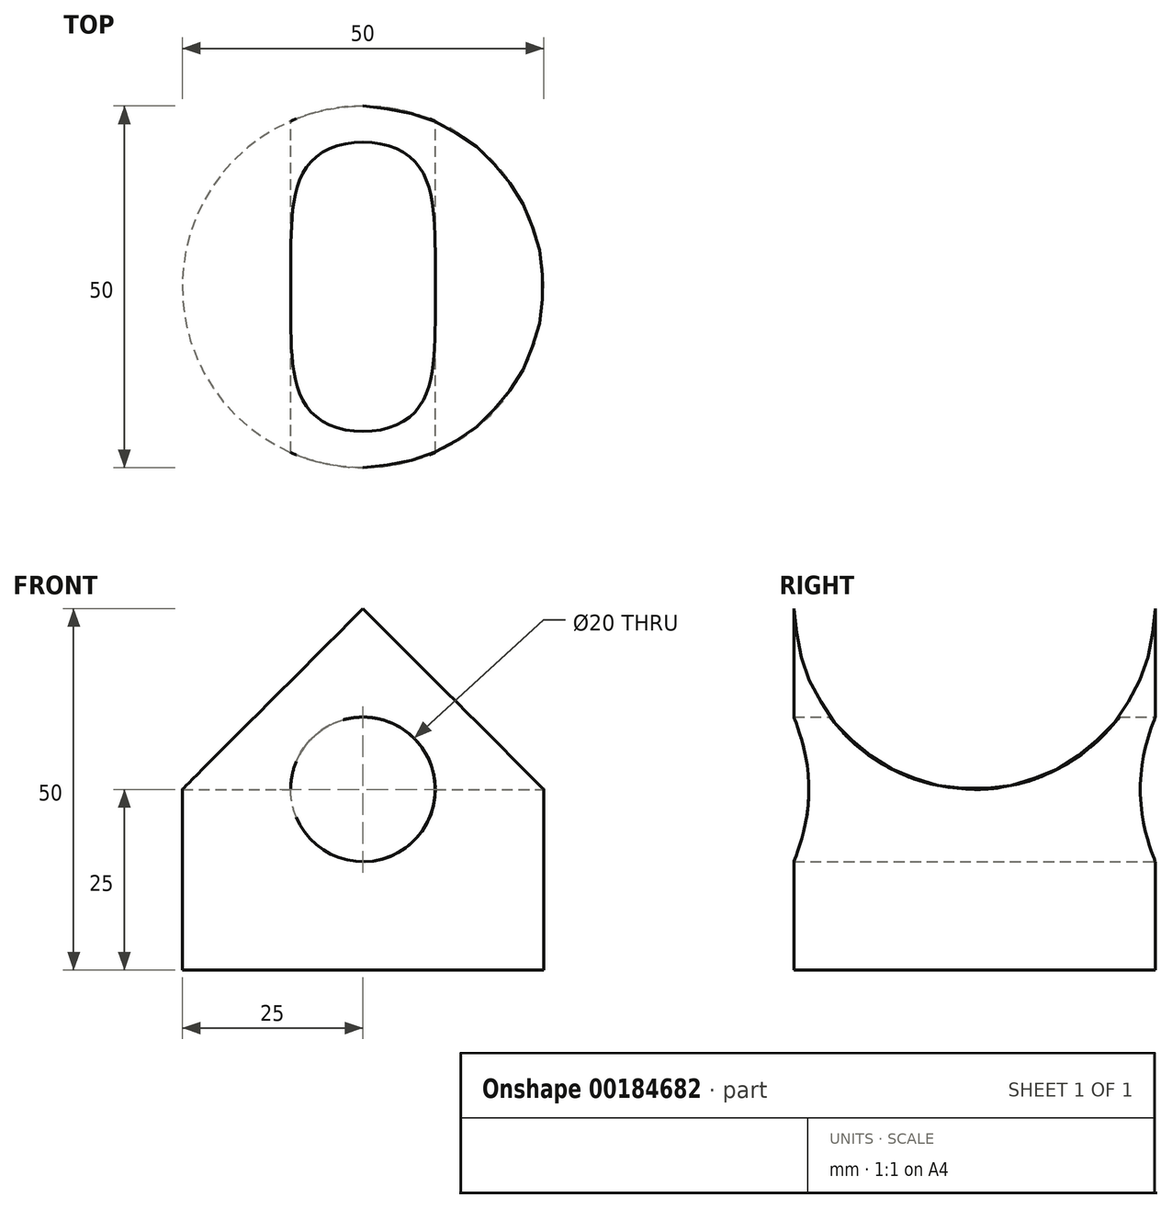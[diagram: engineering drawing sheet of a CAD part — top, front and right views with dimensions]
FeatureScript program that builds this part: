
annotation { "Feature Type Name" : "Feature", "Feature Type Description" : "" }
export const myFeature = defineFeature(function(context is Context, id is Id, definition is map)
    precondition{}
    {
        {
            var Q0;
            Q0=qCreatedBy(makeId("Top.planeOp"),FACE);
            var sketch = newSketch(context, id + "F0", { "sketchPlane" : qUnion([Q0])});
            skCircle(sketch, "E0", {"center": v(0, 0) * mm, "radius": 25 * mm});
            skSolve(sketch);
        }
        {
            var Q0;
            Q0=makeQuery(id+"F0.imprint","IMPRINT",FACE,{"disambiguationData":[TD([[makeQuery(id+"F0.imprint","IMPRINT",EDGE,{"derivedFrom":sQuery(id+"F0.wireOp",EDGE,"E0")}),1.0]])]});
            extrude(context, id + "F1", {"entities" : qUnion([Q0]), "depth" : 50 * mm});
        }
        {
            var Q0;
            Q0=qCreatedBy(makeId("Right.planeOp"),FACE);
            var sketch = newSketch(context, id + "F2", { "sketchPlane" : qUnion([Q0])});
            skLineSegment(sketch, "E1", {"start": v(-25, 0) * mm, "end": v(-25, 50) * mm});
            skLineSegment(sketch, "E2", {"start": v(25, 50) * mm, "end": v(25, 0) * mm});
            skCircle(sketch, "E3", {"center": v(0, 50) * mm, "radius": 25 * mm});
            skSolve(sketch);
        }
        {
            var Q0;
            {var subQ0=sQuery(id+"F2.wireOp",EDGE,"E3");var subQ1=makeQuery(id+"F2.imprint","IMPRINT",VERTEX,{"disambiguationData":[OD(0.0)],"derivedFrom":subQ0});Q0=makeQuery(id+"F2.imprint","IMPRINT",FACE,{"disambiguationData":[TD([[makeQuery(id+"F2.imprint","IMPRINT",EDGE,{"disambiguationData":[TD([[subQ1,1.0]])],"derivedFrom":subQ0}),1.0]])]});}
            extrude(context, id + "F3", {"entities" : qUnion([Q0]), "operationType" : NewBodyOperationType.REMOVE, "endBound" : BoundingType.THROUGH_ALL, "oppositeDirection" : true, "depth" : 25 * mm, "hasSecondDirection" : true, "secondDirectionBound" : BoundingType.THROUGH_ALL, "secondDirectionOppositeDirection" : false, "secondDirectionDepth" : 25 * mm});
        }
        {
            var Q0;
            Q0=qCreatedBy(makeId("Front.planeOp"),FACE);
            var sketch = newSketch(context, id + "F4", { "sketchPlane" : qUnion([Q0])});
            skLineSegment(sketch, "E4", {"start": v(-25, 0) * mm, "end": v(-25, 25) * mm});
            skLineSegment(sketch, "E5", {"start": v(25, 25) * mm, "end": v(25, 0) * mm});
            skCircle(sketch, "E6", {"center": v(0, 25) * mm, "radius": 10 * mm});
            skSolve(sketch);
        }
        {
            var Q0;
            Q0=makeQuery(id+"F4.imprint","IMPRINT",FACE,{"disambiguationData":[TD([[makeQuery(id+"F4.imprint","IMPRINT",EDGE,{"derivedFrom":sQuery(id+"F4.wireOp",EDGE,"E6")}),1.0]])]});
            extrude(context, id + "F5", {"entities" : qUnion([Q0]), "operationType" : NewBodyOperationType.REMOVE, "endBound" : BoundingType.THROUGH_ALL, "depth" : 25 * mm, "hasSecondDirection" : true, "secondDirectionBound" : BoundingType.THROUGH_ALL, "secondDirectionOppositeDirection" : true, "secondDirectionDepth" : 25 * mm});
        }
    });
